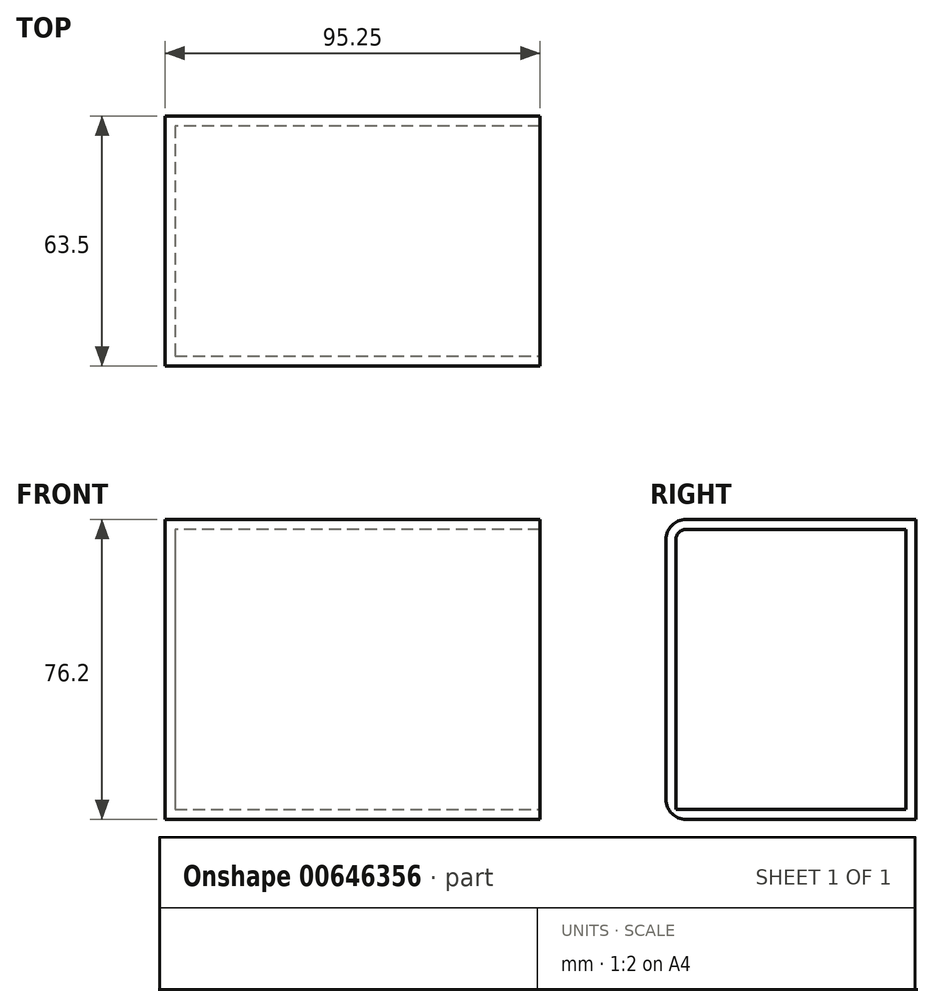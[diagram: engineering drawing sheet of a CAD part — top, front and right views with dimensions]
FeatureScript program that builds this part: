
annotation { "Feature Type Name" : "Feature", "Feature Type Description" : "" }
export const myFeature = defineFeature(function(context is Context, id is Id, definition is map)
    precondition{}
    {
        {
            var Q0;
            Q0=qCreatedBy(makeId("Top.planeOp"),FACE);
            var sketch = newSketch(context, id + "F0", { "sketchPlane" : qUnion([Q0])});
            skLineSegment(sketch, "E0", {"start": v(0, 0) * mm, "end": v(95.25, 0) * mm});
            skLineSegment(sketch, "E1", {"start": v(95.25, 0) * mm, "end": v(95.25, 63.5) * mm});
            skLineSegment(sketch, "E2", {"start": v(95.25, 63.5) * mm, "end": v(0, 63.5) * mm});
            skLineSegment(sketch, "E3", {"start": v(0, 63.5) * mm, "end": v(0, 0) * mm});
            skSolve(sketch);
        }
        {
            var Q0;
            Q0 = qSketchRegion(id + "F0", true);
            extrude(context, id + "F1", {"entities" : qUnion([Q0]), "depth" : 76.2 * mm, "offsetDistance" : 25.4 * mm});
        }
        {
            var Q0;
            Q0=makeQuery(id+"F1.opExtrude","CAP_EDGE",EDGE,{"disambiguationData":[OSD([sQuery(id+"F0.wireOp",EDGE,"E0")])],"isStart":false});
            fillet(context, id + "F2", {"entities" : qUnion([Q0]), "radius" : 5.08 * mm, "tangentPropagation" : true, "allowEdgeOverflow" : false});
        }
        {
            var Q0;
            Q0=makeQuery(id+"F1.opExtrude","SWEPT_FACE",FACE,{"disambiguationData":[OSD([sQuery(id+"F0.wireOp",EDGE,"E1")])]});
            shell(context, id + "F3", {"entities" : qUnion([Q0]), "thickness" : 2.54 * mm});
        }
        {
            var Q0;
            Q0=makeQuery(id+"F1.opExtrude","CAP_EDGE",EDGE,{"disambiguationData":[OSD([sQuery(id+"F0.wireOp",EDGE,"E0")])],"isStart":true});
            fillet(context, id + "F4", {"entities" : qUnion([Q0]), "radius" : 5.08 * mm, "tangentPropagation" : true, "allowEdgeOverflow" : false});
        }
    });
